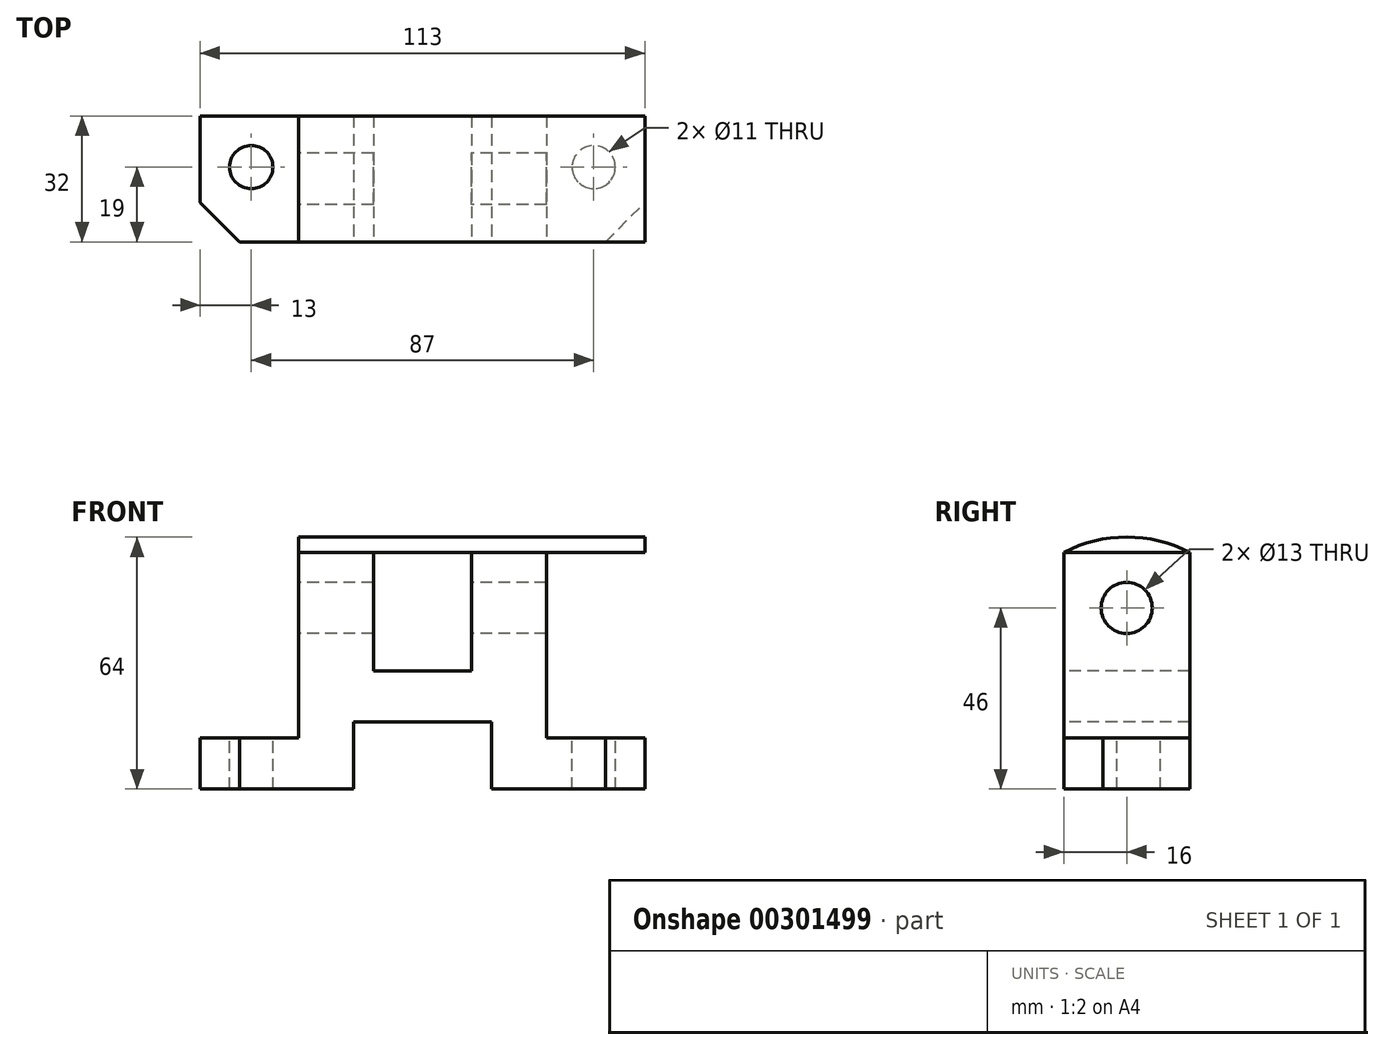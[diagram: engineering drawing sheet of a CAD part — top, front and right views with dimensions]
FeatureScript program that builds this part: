
annotation { "Feature Type Name" : "Feature", "Feature Type Description" : "" }
export const myFeature = defineFeature(function(context is Context, id is Id, definition is map)
    precondition{}
    {
        {
            var Q0;
            Q0=qCreatedBy(makeId("Right.planeOp"),FACE);
            var sketch = newSketch(context, id + "F0", { "sketchPlane" : qUnion([Q0])});
            skLineSegment(sketch, "E0", {"start": v(0, 0) * mm, "end": v(0, 64) * mm});
            skLineSegment(sketch, "E1", {"start": v(32, 64) * mm, "end": v(32, 0) * mm});
            skLineSegment(sketch, "E2", {"start": v(32, 0) * mm, "end": v(0, 0) * mm});
            skLineSegment(sketch, "E3", {"start": v(0, 64) * mm, "end": v(32, 64) * mm});
            skArc(sketch, "E4", {"start": v(32, 60.13) * mm, "mid": v(16, 64) * mm, "end": v(0, 60.13) * mm});
            skLineSegment(sketch, "E5", {"start": v(16, 0) * mm, "end": v(16, 68.9) * mm, "construction": true});
            skCircle(sketch, "E6", {"center": v(16, 46) * mm, "radius": 6.5 * mm});
            skSolve(sketch);
        }
        {
            var Q0;
            {var subQ4=sQuery(id+"F0.wireOp",EDGE,"E2");Q0=makeQuery(id+"F0.imprint","IMPRINT",FACE,{"disambiguationData":[TD([[makeQuery(id+"F0.imprint","IMPRINT",EDGE,{"derivedFrom":subQ4}),-1.0]])]});}
            extrude(context, id + "F1", {"entities" : qUnion([Q0]), "depth" : 113 * mm});
        }
        {
            var Q0;
            Q0=makeQuery(id+"F1.opExtrude","SWEPT_FACE",FACE,{"disambiguationData":[OSD([sQuery(id+"F0.wireOp",EDGE,"E0")])]});
            var sketch = newSketch(context, id + "F2", { "sketchPlane" : qUnion([Q0])});
            skLineSegment(sketch, "E7.bottom", {"start": v(74, 0) * mm, "end": v(39, 0) * mm});
            skLineSegment(sketch, "E7.top", {"start": v(74, 17) * mm, "end": v(39, 17) * mm});
            skLineSegment(sketch, "E7.left", {"start": v(74, 0) * mm, "end": v(74, 17) * mm});
            skLineSegment(sketch, "E7.right", {"start": v(39, 0) * mm, "end": v(39, 17) * mm});
            skLineSegment(sketch, "E8.bottom", {"start": v(44, 64) * mm, "end": v(69, 64) * mm});
            skLineSegment(sketch, "E8.top", {"start": v(44, 30) * mm, "end": v(69, 30) * mm});
            skLineSegment(sketch, "E8.left", {"start": v(44, 64) * mm, "end": v(44, 30) * mm});
            skLineSegment(sketch, "E8.right", {"start": v(69, 64) * mm, "end": v(69, 30) * mm});
            skLineSegment(sketch, "E9.bottom", {"start": v(113, 64) * mm, "end": v(88, 64) * mm});
            skLineSegment(sketch, "E9.top", {"start": v(113, 13) * mm, "end": v(88, 13) * mm});
            skLineSegment(sketch, "E9.left", {"start": v(113, 64) * mm, "end": v(113, 13) * mm});
            skLineSegment(sketch, "E9.right", {"start": v(88, 64) * mm, "end": v(88, 13) * mm});
            skLineSegment(sketch, "E10", {"start": v(0, 64) * mm, "end": v(113, 64) * mm});
            skLineSegment(sketch, "E11.bottom", {"start": v(0, 64) * mm, "end": v(25, 64) * mm});
            skLineSegment(sketch, "E11.top", {"start": v(0, 13) * mm, "end": v(25, 13) * mm});
            skLineSegment(sketch, "E11.left", {"start": v(0, 64) * mm, "end": v(0, 13) * mm});
            skLineSegment(sketch, "E11.right", {"start": v(25, 64) * mm, "end": v(25, 13) * mm});
            skSolve(sketch);
        }
        {
            var Q0;
            {var subQ0=sQuery(id+"F2.wireOp",EDGE,"E11.top");Q0=makeQuery(id+"F2.imprint","IMPRINT",FACE,{"disambiguationData":[TD([[makeQuery(id+"F2.imprint","IMPRINT",EDGE,{"derivedFrom":subQ0}),1.0]])]});}
            var Q1;
            Q1=makeQuery(id+"F2.imprint","IMPRINT",FACE,{"disambiguationData":[TD([[makeQuery(id+"F2.imprint","IMPRINT",EDGE,{"derivedFrom":sQuery(id+"F2.wireOp",EDGE,"E7.bottom")}),-1.0]])]});
            var Q2;
            {var subQ0=sQuery(id+"F2.wireOp",EDGE,"E9.top");Q2=makeQuery(id+"F2.imprint","IMPRINT",FACE,{"disambiguationData":[TD([[makeQuery(id+"F2.imprint","IMPRINT",EDGE,{"derivedFrom":subQ0}),-1.0]])]});}
            var Q3;
            {var subQ0=sQuery(id+"F2.wireOp",EDGE,"E8.top");Q3=makeQuery(id+"F2.imprint","IMPRINT",FACE,{"disambiguationData":[TD([[makeQuery(id+"F2.imprint","IMPRINT",EDGE,{"derivedFrom":subQ0}),1.0]])]});}
            var Q4;
            {var subQ0=sQuery(id+"F2.wireOp",EDGE,"E11.bottom");Q4=makeQuery(id+"F2.imprint","IMPRINT",FACE,{"disambiguationData":[TD([[makeQuery(id+"F2.imprint","IMPRINT",EDGE,{"derivedFrom":subQ0}),-1.0]])]});}
            var Q5;
            {var subQ0=sQuery(id+"F2.wireOp",EDGE,"E10");var subQ1=sQuery(id+"F2.wireOp",EDGE,"E8.left");var subQ2=makeQuery(id+"F2.imprint","INTERSECT",VERTEX,{"derivedFrom":[subQ1,subQ0]});Q5=makeQuery(id+"F2.imprint","IMPRINT",FACE,{"disambiguationData":[TD([[makeQuery(id+"F2.imprint","IMPRINT",EDGE,{"disambiguationData":[TD([[subQ2,-1.0]])],"derivedFrom":subQ0}),-1.0]])]});}
            var Q6;
            {var subQ0=sQuery(id+"F2.wireOp",EDGE,"E9.left");var subQ3=sQuery(id+"F2.wireOp",EDGE,"E10");var subQ4=makeQuery(id+"F2.imprint","INTERSECT",VERTEX,{"derivedFrom":[subQ0,subQ3]});Q6=makeQuery(id+"F2.imprint","IMPRINT",FACE,{"disambiguationData":[TD([[makeQuery(id+"F2.imprint","IMPRINT",EDGE,{"disambiguationData":[TD([[subQ4,1.0]])],"derivedFrom":subQ3}),-1.0]])]});}
            extrude(context, id + "F3", {"entities" : qUnion([Q0, Q1, Q2, Q3, Q4, Q5, Q6]), "operationType" : NewBodyOperationType.REMOVE, "endBound" : BoundingType.THROUGH_ALL, "oppositeDirection" : true, "depth" : 25 * mm});
        }
        {
            var Q0;
            Q0=makeQuery(id+"F3.boolean.opBoolean","COPY",FACE,{"derivedFrom":makeQuery(id+"F3.opExtrude","SWEPT_FACE",FACE,{"disambiguationData":[OSD([sQuery(id+"F2.wireOp",EDGE,"E9.top")])]})});
            var sketch = newSketch(context, id + "F4", { "sketchPlane" : qUnion([Q0])});
            skCircle(sketch, "E12", {"center": v(100, 19) * mm, "radius": 5.5 * mm});
            skCircle(sketch, "E13", {"center": v(13, 19) * mm, "radius": 5.5 * mm});
            skSolve(sketch);
        }
        {
            var Q0;
            Q0=makeQuery(id+"F4.imprint","IMPRINT",FACE,{"disambiguationData":[TD([[makeQuery(id+"F4.imprint","IMPRINT",EDGE,{"derivedFrom":sQuery(id+"F4.wireOp",EDGE,"EaMY3Bng-NMgD-BB4d-am1r-O0kgqUzUDVIX")}),1.0]])]});
            var Q1;
            Q1=makeQuery(id+"F4.imprint","IMPRINT",FACE,{"disambiguationData":[TD([[makeQuery(id+"F4.imprint","IMPRINT",EDGE,{"derivedFrom":sQuery(id+"F4.wireOp",EDGE,"E12")}),1.0]])]});
            var Q2;
            Q2=makeQuery(id+"F4.imprint","IMPRINT",FACE,{"disambiguationData":[TD([[makeQuery(id+"F4.imprint","IMPRINT",EDGE,{"derivedFrom":sQuery(id+"F4.wireOp",EDGE,"E13")}),1.0]])]});
            extrude(context, id + "F5", {"entities" : qUnion([Q0, Q1, Q2]), "operationType" : NewBodyOperationType.REMOVE, "endBound" : BoundingType.THROUGH_ALL, "oppositeDirection" : true, "depth" : 25 * mm});
        }
        {
            var Q0;
            Q0=makeQuery(id+"F1.opExtrude","CAP_EDGE",EDGE,{"disambiguationData":[OSD([sQuery(id+"F0.wireOp",EDGE,"E0")])],"isStart":true});
            var Q1;
            Q1=makeQuery(id+"F1.opExtrude","CAP_EDGE",EDGE,{"disambiguationData":[OSD([sQuery(id+"F0.wireOp",EDGE,"E0")])],"isStart":false});
            chamfer(context, id + "F6", {"entities" : qUnion([Q0, Q1]), "width" : 10 * mm, "tangentPropagation" : true});
        }
    });
